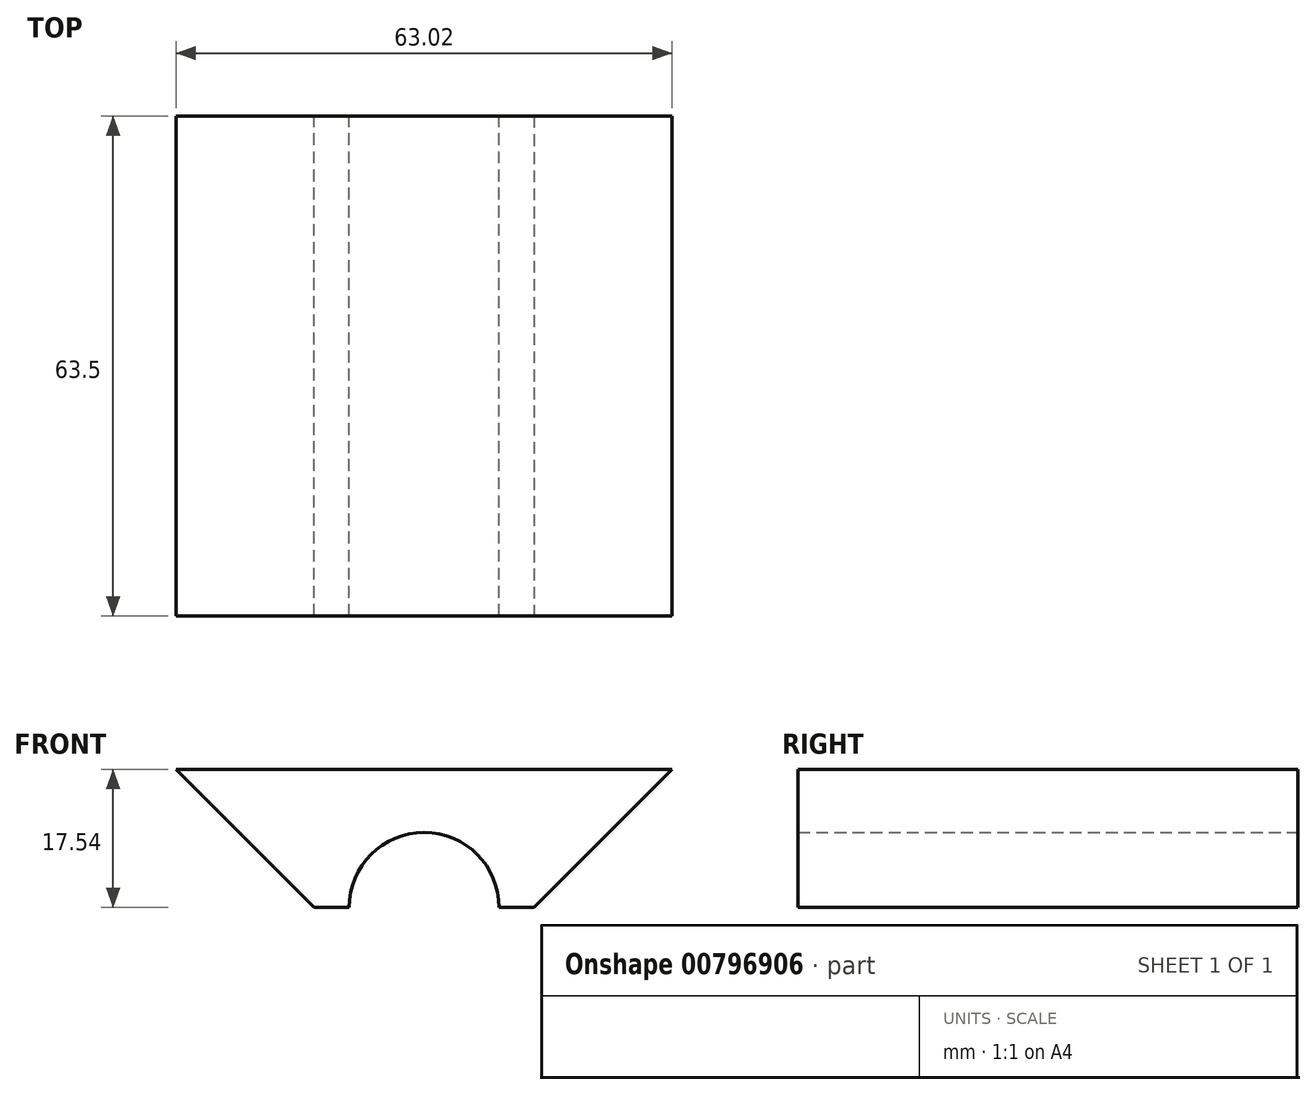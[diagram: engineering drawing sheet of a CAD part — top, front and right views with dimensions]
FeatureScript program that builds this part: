
annotation { "Feature Type Name" : "Feature", "Feature Type Description" : "" }
export const myFeature = defineFeature(function(context is Context, id is Id, definition is map)
    precondition{}
    {
        {
            var Q0;
            Q0=qCreatedBy(makeId("Front.planeOp"),FACE);
            var sketch = newSketch(context, id + "F0", { "sketchPlane" : qUnion([Q0])});
            skCircle(sketch, "E0", {"center": v(0, 0) * mm, "radius": 9.53 * mm});
            skSolve(sketch);
        }
        {
            var Q0;
            Q0=makeQuery(id+"F0.imprint","IMPRINT",FACE,{"disambiguationData":[TD([[makeQuery(id+"F0.imprint","IMPRINT",EDGE,{"derivedFrom":sQuery(id+"F0.wireOp",EDGE,"E0")}),1.0]])]});
            var sketch = newSketch(context, id + "F1", { "sketchPlane" : qUnion([Q0])});
            skLineSegment(sketch, "E1", {"start": v(-17.95, 0) * mm, "end": v(17.97, 0) * mm});
            skLineSegment(sketch, "E2.bottom", {"start": v(31.75, 0) * mm, "end": v(-31.75, 0) * mm});
            skLineSegment(sketch, "E2.top", {"start": v(31.75, 17.54) * mm, "end": v(-31.75, 17.54) * mm});
            skLineSegment(sketch, "E2.left", {"start": v(31.75, 0) * mm, "end": v(31.75, 17.54) * mm});
            skLineSegment(sketch, "E2.right", {"start": v(-31.75, 0) * mm, "end": v(-31.75, 17.54) * mm});
            skPoint(sketch, "E2.middle", {"position": v(0, 8.77) * mm});
            skSolve(sketch);
        }
        {
            var Q0;
            Q0=makeQuery(id+"F1.imprint","IMPRINT",FACE,{"disambiguationData":[TD([[makeQuery(id+"F1.imprint","IMPRINT",EDGE,{"derivedFrom":sQuery(id+"F1.wireOp",EDGE,"E2.top")}),1.0]])]});
            extrude(context, id + "F2", {"entities" : qUnion([Q0]), "depth" : 63.5 * mm, "offsetDistance" : 25.4 * mm});
        }
        {
            var Q0;
            Q0=makeQuery(id+"F2.opExtrude","SWEPT_EDGE",EDGE,{"disambiguationData":[OSD([sQuery(id+"F1.wireOp",EDGE,"E2.bottom"),sQuery(id+"F1.wireOp",EDGE,"E2.right")])]});
            var Q1;
            Q1=makeQuery(id+"F2.opExtrude","SWEPT_EDGE",EDGE,{"disambiguationData":[OSD([sQuery(id+"F1.wireOp",EDGE,"E2.bottom"),sQuery(id+"F1.wireOp",EDGE,"E2.left")])]});
            chamfer(context, id + "F3", {"entities" : qUnion([Q0, Q1]), "width" : 17.78 * mm, "tangentPropagation" : true});
        }
    });
